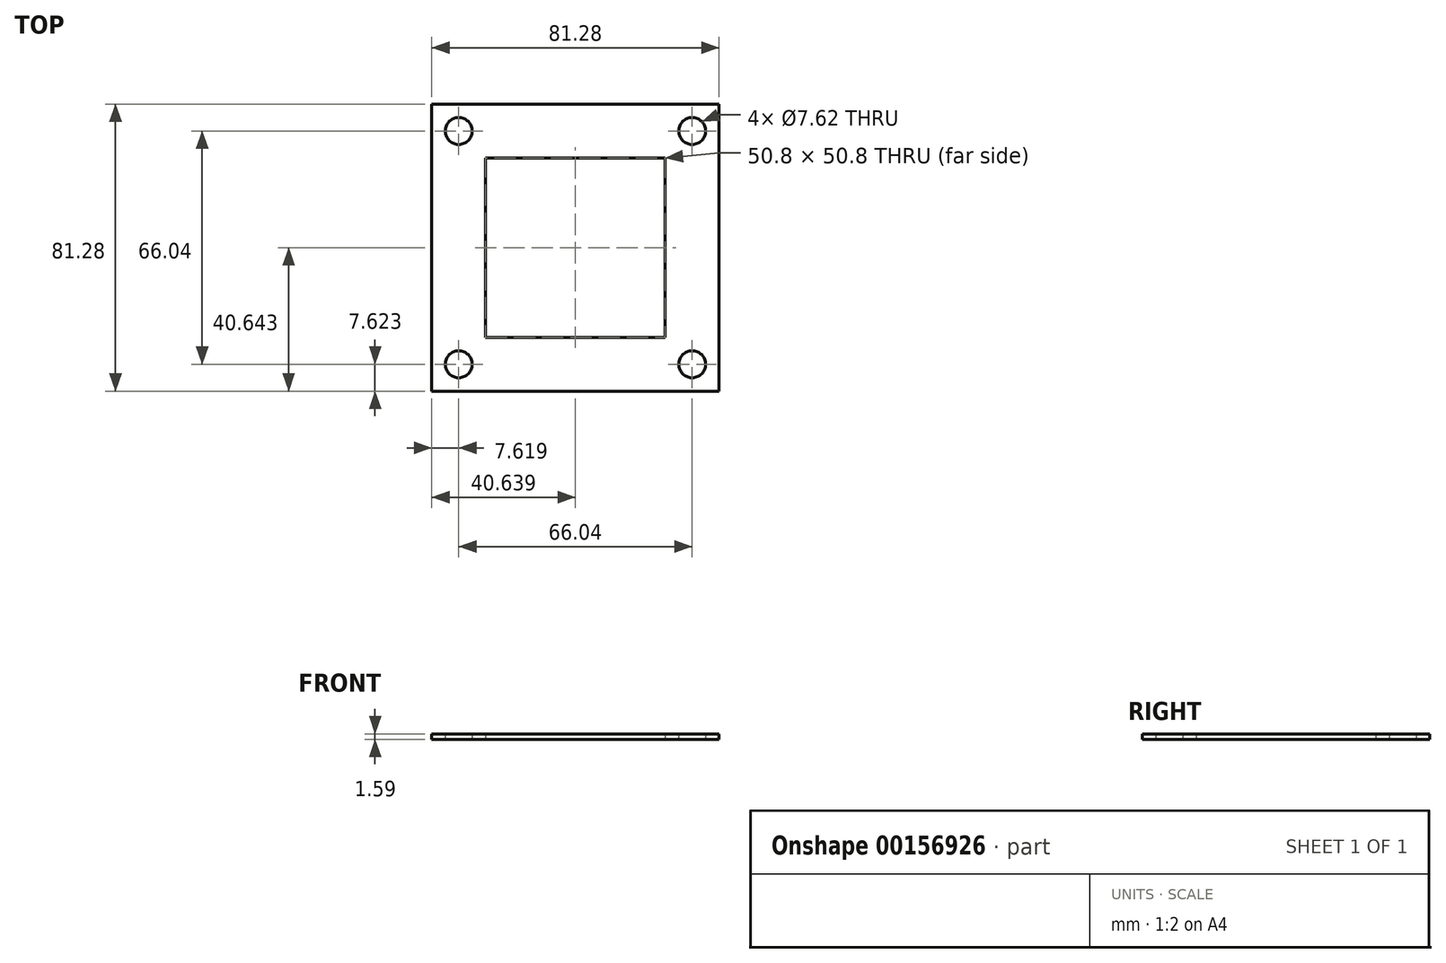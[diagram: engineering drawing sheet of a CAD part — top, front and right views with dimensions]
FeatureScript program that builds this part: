
annotation { "Feature Type Name" : "Feature", "Feature Type Description" : "" }
export const myFeature = defineFeature(function(context is Context, id is Id, definition is map)
    precondition{}
    {
        {
            var Q0;
            Q0=qCreatedBy(makeId("Top.planeOp"),FACE);
            var sketch = newSketch(context, id + "F0", { "sketchPlane" : qUnion([Q0])});
            skLineSegment(sketch, "E0.bottom", {"start": v(-31.71, 9.78) * mm, "end": v(19.09, 9.78) * mm});
            skLineSegment(sketch, "E0.top", {"start": v(-31.71, -41.02) * mm, "end": v(19.09, -41.02) * mm});
            skLineSegment(sketch, "E0.left", {"start": v(-31.71, 9.78) * mm, "end": v(-31.71, -41.02) * mm});
            skLineSegment(sketch, "E0.right", {"start": v(19.09, 9.78) * mm, "end": v(19.09, -41.02) * mm});
            skLineSegment(sketch, "E1.bottom", {"start": v(-46.95, 25.02) * mm, "end": v(34.33, 25.02) * mm});
            skLineSegment(sketch, "E1.top", {"start": v(-46.95, -56.26) * mm, "end": v(34.33, -56.26) * mm});
            skLineSegment(sketch, "E1.left", {"start": v(-46.95, 25.02) * mm, "end": v(-46.95, -56.26) * mm});
            skLineSegment(sketch, "E1.right", {"start": v(34.33, 25.02) * mm, "end": v(34.33, -56.26) * mm});
            skLineSegment(sketch, "E2.bottom", {"start": v(19.09, -41.02) * mm, "end": v(34.33, -41.02) * mm});
            skLineSegment(sketch, "E2.top", {"start": v(19.09, -56.26) * mm, "end": v(34.33, -56.26) * mm});
            skLineSegment(sketch, "E2.left", {"start": v(19.09, -41.02) * mm, "end": v(19.09, -56.26) * mm});
            skLineSegment(sketch, "E2.right", {"start": v(34.33, -41.02) * mm, "end": v(34.33, -56.26) * mm});
            skLineSegment(sketch, "E3.bottom", {"start": v(-31.71, -41.02) * mm, "end": v(-46.95, -41.02) * mm});
            skLineSegment(sketch, "E3.top", {"start": v(-31.71, -56.26) * mm, "end": v(-46.95, -56.26) * mm});
            skLineSegment(sketch, "E3.left", {"start": v(-31.71, -41.02) * mm, "end": v(-31.71, -56.26) * mm});
            skLineSegment(sketch, "E3.right", {"start": v(-46.95, -41.02) * mm, "end": v(-46.95, -56.26) * mm});
            skLineSegment(sketch, "E4.bottom", {"start": v(-31.71, 9.78) * mm, "end": v(-46.95, 9.78) * mm});
            skLineSegment(sketch, "E4.top", {"start": v(-31.71, 25.02) * mm, "end": v(-46.95, 25.02) * mm});
            skLineSegment(sketch, "E4.left", {"start": v(-31.71, 9.78) * mm, "end": v(-31.71, 25.02) * mm});
            skLineSegment(sketch, "E4.right", {"start": v(-46.95, 9.78) * mm, "end": v(-46.95, 25.02) * mm});
            skLineSegment(sketch, "E5.bottom", {"start": v(19.09, 9.78) * mm, "end": v(34.33, 9.78) * mm});
            skLineSegment(sketch, "E5.top", {"start": v(19.09, 25.02) * mm, "end": v(34.33, 25.02) * mm});
            skLineSegment(sketch, "E5.left", {"start": v(19.09, 9.78) * mm, "end": v(19.09, 25.02) * mm});
            skLineSegment(sketch, "E5.right", {"start": v(34.33, 9.78) * mm, "end": v(34.33, 25.02) * mm});
            skCircle(sketch, "E6", {"center": v(-39.33, -48.64) * mm, "radius": 3.81 * mm});
            skCircle(sketch, "E7", {"center": v(-39.33, 17.4) * mm, "radius": 3.81 * mm});
            skCircle(sketch, "E8", {"center": v(26.7, 17.4) * mm, "radius": 3.81 * mm});
            skCircle(sketch, "E9", {"center": v(26.7, -48.64) * mm, "radius": 3.81 * mm});
            skSolve(sketch);
        }
        {
            var Q0;
            {var subQ1=sQuery(id+"F0.wireOp",EDGE,"E3.top");Q0=makeQuery(id+"F0.imprint","IMPRINT",FACE,{"disambiguationData":[TD([[makeQuery(id+"F0.imprint","IMPRINT",EDGE,{"derivedFrom":subQ1}),-1.0]])]});}
            var Q1;
            Q1=makeQuery(id+"F0.imprint","IMPRINT",FACE,{"disambiguationData":[TD([[makeQuery(id+"F0.imprint","IMPRINT",EDGE,{"derivedFrom":sQuery(id+"F0.wireOp",EDGE,"E2.bottom")}),-1.0]])]});
            var Q2;
            Q2=makeQuery(id+"F0.imprint","IMPRINT",FACE,{"disambiguationData":[TD([[makeQuery(id+"F0.imprint","IMPRINT",EDGE,{"derivedFrom":sQuery(id+"F0.wireOp",EDGE,"E2.top")}),1.0]])]});
            var Q3;
            Q3=makeQuery(id+"F0.imprint","IMPRINT",FACE,{"disambiguationData":[TD([[makeQuery(id+"F0.imprint","IMPRINT",EDGE,{"derivedFrom":sQuery(id+"F0.wireOp",EDGE,"E4.bottom")}),-1.0]])]});
            var Q4;
            Q4=makeQuery(id+"F0.imprint","IMPRINT",FACE,{"disambiguationData":[TD([[makeQuery(id+"F0.imprint","IMPRINT",EDGE,{"derivedFrom":sQuery(id+"F0.wireOp",EDGE,"E4.top")}),1.0]])]});
            var Q5;
            Q5=makeQuery(id+"F0.imprint","IMPRINT",FACE,{"disambiguationData":[TD([[makeQuery(id+"F0.imprint","IMPRINT",EDGE,{"derivedFrom":sQuery(id+"F0.wireOp",EDGE,"E5.bottom")}),1.0]])]});
            var Q6;
            Q6=makeQuery(id+"F0.imprint","IMPRINT",FACE,{"disambiguationData":[TD([[makeQuery(id+"F0.imprint","IMPRINT",EDGE,{"derivedFrom":sQuery(id+"F0.wireOp",EDGE,"E5.top")}),-1.0]])]});
            var Q7;
            {var subQ0=sQuery(id+"F0.wireOp",EDGE,"E6");var subQ1=sQuery(id+"F0.wireOp",EDGE,"6TTmRBJs-6HWV-zHlN-zFCb-LBSHuJk2n4DZ");var subQ2=makeQuery(id+"F0.imprint","INTERSECT",VERTEX,{"disambiguationData":[OD(0.0)],"derivedFrom":[subQ1,subQ0]});Q7=makeQuery(id+"F0.imprint","IMPRINT",FACE,{"disambiguationData":[TD([[makeQuery(id+"F0.imprint","IMPRINT",EDGE,{"disambiguationData":[TD([[subQ2,-1.0]])],"derivedFrom":subQ1}),-1.0]])]});}
            var Q8;
            {var subQ0=sQuery(id+"F0.wireOp",EDGE,"E6");var subQ1=sQuery(id+"F0.wireOp",EDGE,"6TTmRBJs-6HWV-zHlN-zFCb-LBSHuJk2n4DZ");var subQ2=makeQuery(id+"F0.imprint","INTERSECT",VERTEX,{"disambiguationData":[OD(0.0)],"derivedFrom":[subQ1,subQ0]});Q8=makeQuery(id+"F0.imprint","IMPRINT",FACE,{"disambiguationData":[TD([[makeQuery(id+"F0.imprint","IMPRINT",EDGE,{"disambiguationData":[TD([[subQ2,-1.0]])],"derivedFrom":subQ1}),1.0]])]});}
            var Q9;
            Q9=makeQuery(id+"F0.imprint","IMPRINT",FACE,{"disambiguationData":[TD([[makeQuery(id+"F0.imprint","IMPRINT",EDGE,{"derivedFrom":sQuery(id+"F0.wireOp",EDGE,"E0.bottom")}),1.0]])]});
            var Q10;
            Q10=makeQuery(id+"F0.imprint","IMPRINT",FACE,{"disambiguationData":[TD([[makeQuery(id+"F0.imprint","IMPRINT",EDGE,{"derivedFrom":sQuery(id+"F0.wireOp",EDGE,"E0.top")}),-1.0]])]});
            var Q11;
            Q11=makeQuery(id+"F0.imprint","IMPRINT",FACE,{"disambiguationData":[TD([[makeQuery(id+"F0.imprint","IMPRINT",EDGE,{"derivedFrom":sQuery(id+"F0.wireOp",EDGE,"E0.left")}),-1.0]])]});
            var Q12;
            Q12=makeQuery(id+"F0.imprint","IMPRINT",FACE,{"disambiguationData":[TD([[makeQuery(id+"F0.imprint","IMPRINT",EDGE,{"derivedFrom":sQuery(id+"F0.wireOp",EDGE,"E0.right")}),1.0]])]});
            var Q13;
            {var subQ4=sQuery(id+"F0.wireOp",EDGE,"E3.bottom");Q13=makeQuery(id+"F0.imprint","IMPRINT",FACE,{"disambiguationData":[TD([[makeQuery(id+"F0.imprint","IMPRINT",EDGE,{"derivedFrom":subQ4}),1.0]])]});}
            extrude(context, id + "F1", {"entities" : qUnion([Q0, Q1, Q2, Q3, Q4, Q5, Q6, Q7, Q8, Q9, Q10, Q11, Q12, Q13]), "depth" : 1.59 * mm});
        }
    });
